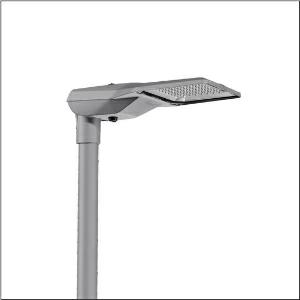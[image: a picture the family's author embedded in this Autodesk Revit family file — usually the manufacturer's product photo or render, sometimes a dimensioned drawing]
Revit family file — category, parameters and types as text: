
# Revit family: streetlight_sl_21_iq_midi___stw1_0a_5xe3e31y08mb_1dd4
name_source: partatom
category: Lighting Fixtures
units: mm (PartAtom-declared; Revit-internal decimal feet)

## family parameters
Cut with Voids When Loaded = No
Host = Face
Light Source = No
Part Type = Normal
Room Calculation Point = No
Round Connector Dimension = Use Diameter
Shared = No

## types (1)
- --- (1 x LED, 18340 lm, 129.3 W, 3000K)
    Apparent Load = 129 VA
    CIE Flux Codes = 38 75 98 100 100
    Color Rendering = 70
    Color Temperature = 3000K
    Default Elevation = 1800 mm
    Description = Streetlight SL 21 iQ midi, mast luminaire, primary light control with lens, of PMMA, primary optical cover: cover, of toughened safety glass, transparent, light distribution: STW1.0a, light emission: direct distribution, primary light characteristic: asymmetric, installation type: post-top, side-entry, LED, High Power LED, rated luminous flux: 18.340lm, luminous efficacy: 142lm/W, light colour: 730, colour temperature: 3000K, control: presetting dimming logarithmic, Street-Remote, Auto-Match, Temp-Guard, Lumen-Switch, Night-Set, Smart-Wire, Light-Fading, Desk-Remote (wireless, voltage-free reading and setting of iQ features in the workshop via application-optimized NFC function/RFID function), optimised constant luminous flux control (CLO 2.0), mains connection: 230..240V, AC, 50/60Hz, start of lifetime: 129W, end of service life: 142W, reduction: 56W, luminaire housing, of diecast aluminium, powder-coated, Siteco® metallic grey (DB 702S), corrosivity category C5 mid according to DIN EN ISO 12944, please order mast flange separately, inclination adjustable: 0°, 5°, 10°, 15°, sealing non-destructively replaceable, multi-level sealing system, length: 644mm, width: 335mm, height: 110mm, mast flange for spigot size: 42mm (side-entry): 5XC10008XM4, 60/48mm (side-entry/post-top): 5XC10108XM2, 76/60mm (side-entry/post-top): 5XC10108XM1, Smart Interface below and above, protection rating (complete): IP66, insulation class (complete): insulation class II (safety insulation), certification: CE, ENEC, ENEC+, VDE, impact resistance: IK09, permissible operating ambient temperature for outdoor applications: -40..+50°C, standard-compliant lighting for roads and squares, packaging unit: 1 piece

Light Distribution: STW1.0a
    Height = 111 mm
    Lamp = 1 x LED
    Lamp Light Flux = 18340 lm
    Lamp Power = 129.3 W
    Lamp count = 1
    Length = 644 mm
    Luminous efficacy = 142 lm/W
    Manufacturer = Siteco
    ModVariant = No
    Model = 5XE3E31Y08MB
    Number of Poles = 1
    OnlyDefault = Yes
    Power Factor = 1
    Product Name = Streetlight SL 21 iQ midi | STW1.0a
    Product group = mast luminaire | pylon top
    ProductGroupID = 6100
    Protection Class = Protection class II
    Protection Degree = IP 66
    RLX_Detail_Level = 1
    RLX_Emergency_Light_Flux = 0 lm
    RLX_Emergency_Type = 0
    RLX_Emergency_Type_DB = No
    RlxData = <blob elided: 91021 chars, md5=5a18cacf>
    Socket = socket
    Standby Power = 0 W
    System Light Flux = 18340 lm
    System Power = 129 W
    Type Comments = factory setting: luminous flux: 100 % | dim-lin: 254 | 672 mA
    Type Image = l_1004304.jpg
    URL = http://relux.com
    VarID = @adj_062459
    Voltage = 0 V
    Weight = 0.00 kg
    Width = 336 mm

## geometry (parser evidence)
native form markers: Blend x4, Sweep x10
no freeform markers — native parametric forms only
